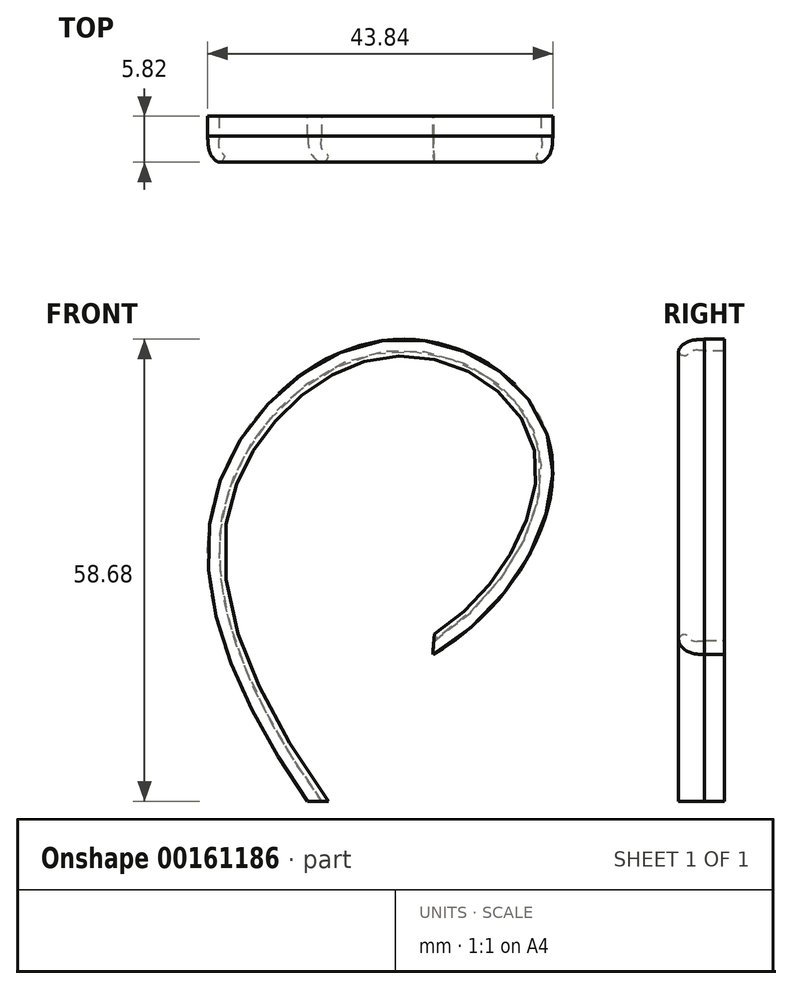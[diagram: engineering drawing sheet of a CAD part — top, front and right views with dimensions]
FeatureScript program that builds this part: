
annotation { "Feature Type Name" : "Feature", "Feature Type Description" : "" }
export const myFeature = defineFeature(function(context is Context, id is Id, definition is map)
    precondition{}
    {
        {
            var Q0;
            Q0=qCreatedBy(makeId("Front.planeOp"),FACE);
            var sketch = newSketch(context, id + "F0", { "sketchPlane" : qUnion([Q0])});
            skFitSpline(sketch, "E0", {"points": [v(0, 0) * mm, v(-12.17, 37.76) * mm, v(9.57, 57.86) * mm, v(29.07, 45.4) * mm, v(15.05, 19.52) * mm], "startDerivative": vector(-91.2, 128.07) * mm, "endDerivative": vector(-114.24, -68.54) * mm});
            skSolve(sketch);
        }
        {
            var Q0;
            Q0=qCreatedBy(makeId("Top.planeOp"),FACE);
            var sketch = newSketch(context, id + "F1", { "sketchPlane" : qUnion([Q0])});
            skLineSegment(sketch, "E1.top", {"start": v(0.9, 1.27) * mm, "end": v(-0.9, 1.27) * mm});
            skLineSegment(sketch, "E1.left", {"start": v(0.9, -1.27) * mm, "end": v(0.9, 1.27) * mm});
            skLineSegment(sketch, "E1.right", {"start": v(-0.9, -1.27) * mm, "end": v(-0.9, 1.27) * mm});
            skPoint(sketch, "E1.middle", {"position": v(0, 0) * mm});
            skFitSpline(sketch, "E2", {"points": [v(-0.9, -1.27) * mm, v(-0.45, -3.54) * mm, v(1.1, -4.54) * mm, v(1.7, -3.74) * mm, v(1.07, -3.18) * mm, v(0.9, -1.27) * mm], "startDerivative": vector(0.6, -10.32) * mm, "endDerivative": vector(2.05, 12.53) * mm});
            skSolve(sketch);
        }
        {
            var Q0;
            Q0=makeQuery(id+"F1.imprint","IMPRINT",FACE,{"disambiguationData":[TD([[makeQuery(id+"F1.imprint","IMPRINT",EDGE,{"derivedFrom":sQuery(id+"F1.wireOp",EDGE,"E1.top")}),1.0]])]});
            var Q1;
            Q1=sQuery(id+"F0.wireOp",EDGE,"E0");
            sweep(context, id + "F2", {"profiles" : qUnion([Q0]), "path" : qUnion([Q1])});
        }
    });
